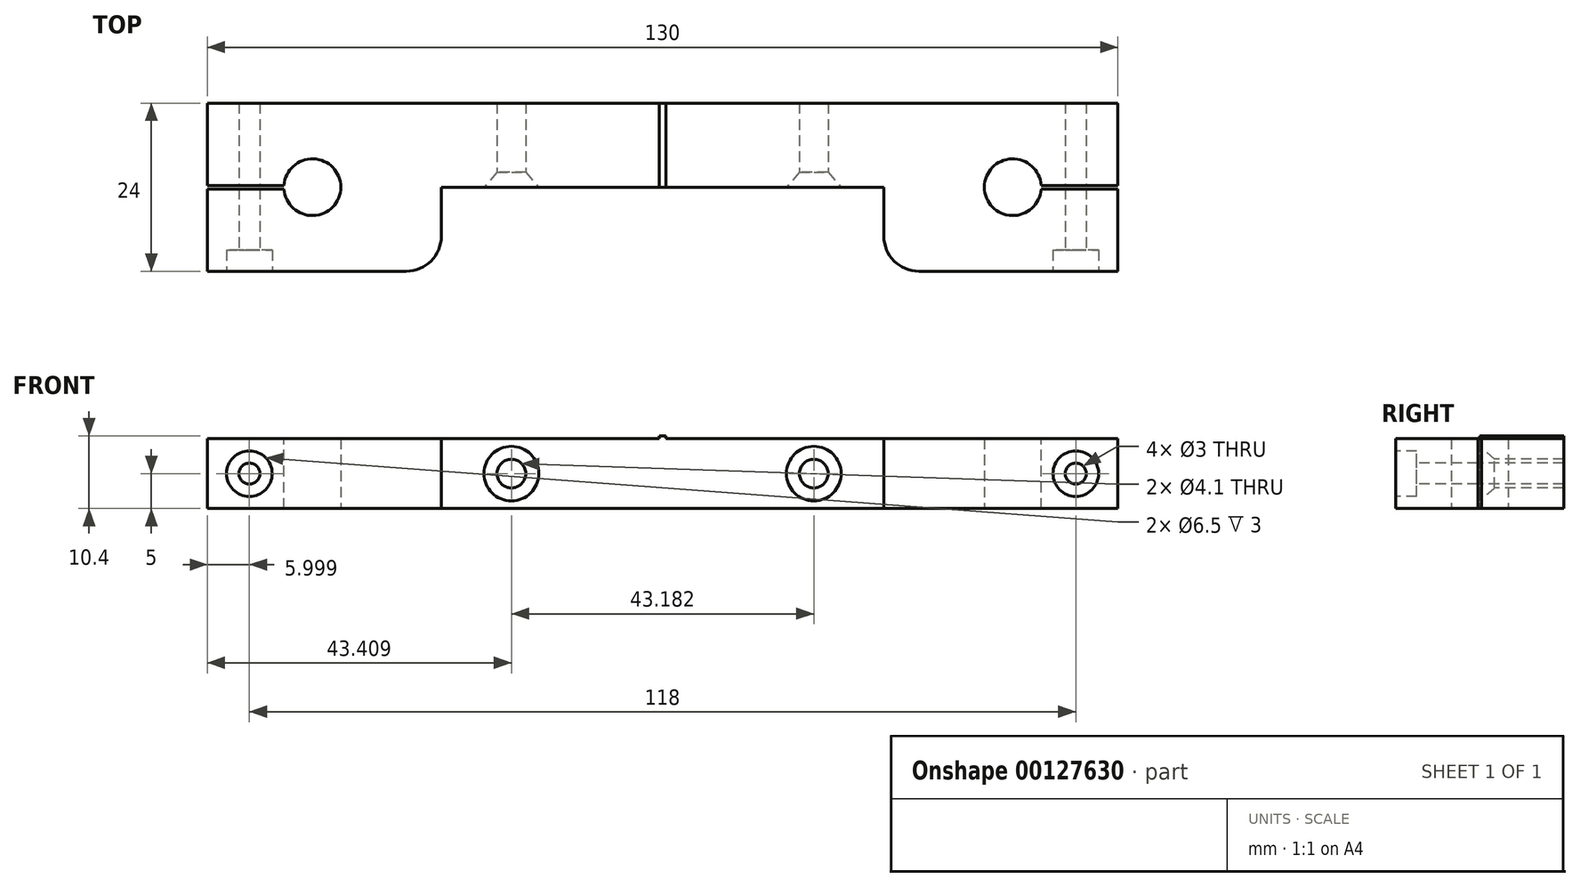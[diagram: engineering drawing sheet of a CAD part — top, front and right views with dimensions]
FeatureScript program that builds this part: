
annotation { "Feature Type Name" : "Feature", "Feature Type Description" : "" }
export const myFeature = defineFeature(function(context is Context, id is Id, definition is map)
    precondition{}
    {
        {
            var Q0;
            Q0=qCreatedBy(makeId("Top.planeOp"),FACE);
            var sketch = newSketch(context, id + "F0", { "sketchPlane" : qUnion([Q0])});
            skLineSegment(sketch, "E0.bottom", {"start": v(-62.4, -8.21) * mm, "end": v(67.6, -8.21) * mm});
            skLineSegment(sketch, "E0.top", {"start": v(-62.4, -32.21) * mm, "end": v(67.6, -32.21) * mm});
            skLineSegment(sketch, "E0.left", {"start": v(-62.4, -8.21) * mm, "end": v(-62.4, -32.21) * mm});
            skLineSegment(sketch, "E0.right", {"start": v(67.6, -8.21) * mm, "end": v(67.6, -32.21) * mm});
            skLineSegment(sketch, "E1", {"start": v(-62.4, -20.21) * mm, "end": v(67.6, -20.21) * mm, "construction": true});
            skLineSegment(sketch, "E2", {"start": v(-47.4, -8.21) * mm, "end": v(-47.4, -32.21) * mm, "construction": true});
            skCircle(sketch, "E3", {"center": v(-47.4, -20.21) * mm, "radius": 4.05 * mm});
            skCircle(sketch, "E4.1.0.0", {"center": v(52.6, -20.21) * mm, "radius": 4.05 * mm});
            skLineSegment(sketch, "E4.direction1", {"start": v(-47.4, -20.21) * mm, "end": v(52.6, -20.21) * mm, "construction": true});
            skPoint(sketch, "E5", {"position": v(2.6, -32.21) * mm});
            skLineSegment(sketch, "E6.bottom", {"start": v(-29, -32.21) * mm, "end": v(34.2, -32.21) * mm});
            skLineSegment(sketch, "E6.top", {"start": v(-29, -20.21) * mm, "end": v(34.2, -20.21) * mm});
            skLineSegment(sketch, "E6.left", {"start": v(-29, -32.21) * mm, "end": v(-29, -20.21) * mm});
            skLineSegment(sketch, "E6.right", {"start": v(34.2, -32.21) * mm, "end": v(34.2, -20.21) * mm});
            skPoint(sketch, "E7", {"position": v(2.6, -20.21) * mm});
            skSolve(sketch);
        }
        {
            var Q0;
            Q0=makeQuery(id+"F0.imprint","IMPRINT",FACE,{"disambiguationData":[TD([[makeQuery(id+"F0.imprint","IMPRINT",EDGE,{"derivedFrom":sQuery(id+"F0.wireOp",EDGE,"E0.bottom")}),-1.0]])]});
            extrude(context, id + "F1", {"entities" : qUnion([Q0]), "depth" : 10 * mm});
        }
        {
            var Q0;
            Q0=makeQuery(id+"F1.opExtrude","SWEPT_EDGE",EDGE,{"disambiguationData":[OSD([sQuery(id+"F0.wireOp",EDGE,"E0.top"),sQuery(id+"F0.wireOp",EDGE,"E6.bottom"),sQuery(id+"F0.wireOp",EDGE,"E6.right")])]});
            var Q1;
            Q1=makeQuery(id+"F1.opExtrude","SWEPT_EDGE",EDGE,{"disambiguationData":[OSD([sQuery(id+"F0.wireOp",EDGE,"E0.top"),sQuery(id+"F0.wireOp",EDGE,"E6.bottom"),sQuery(id+"F0.wireOp",EDGE,"E6.left")])]});
            fillet(context, id + "F2", {"entities" : qUnion([Q0, Q1]), "radius" : 5 * mm, "tangentPropagation" : true, "allowEdgeOverflow" : false});
        }
        {
            var Q0;
            Q0=makeQuery(id+"F1.opExtrude","SWEPT_FACE",FACE,{"disambiguationData":[OSD([sQuery(id+"F0.wireOp",EDGE,"E6.top")])]});
            var sketch = newSketch(context, id + "F3", { "sketchPlane" : qUnion([Q0])});
            skLineSegment(sketch, "E8", {"start": v(-29, 5) * mm, "end": v(34.2, 5) * mm, "construction": true});
            skLineSegment(sketch, "E9", {"start": v(-19, 10) * mm, "end": v(-19, 0) * mm, "construction": true});
            skLineSegment(sketch, "E10", {"start": v(24.2, 10) * mm, "end": v(24.2, 0) * mm, "construction": true});
            skPoint(sketch, "E11", {"position": v(-19, 5) * mm});
            skPoint(sketch, "E12", {"position": v(24.2, 5) * mm});
            skSolve(sketch);
        }
        {
            var Q0;
            Q0=sQuery(id+"F3.wireOp",VERTEX,"E11");
            var Q1;
            Q1=sQuery(id+"F3.wireOp",VERTEX,"E12");
            var Q2;
            Q2=makeQuery(id+"F1.opExtrude","SWEPT_BODY",BODY,{"disambiguationData":[OSD([sQuery(id+"F0.wireOp",EDGE,"E0.bottom"),sQuery(id+"F0.wireOp",EDGE,"E0.top"),sQuery(id+"F0.wireOp",EDGE,"E0.left"),sQuery(id+"F0.wireOp",EDGE,"E0.right"),sQuery(id+"F0.wireOp",EDGE,"E3"),sQuery(id+"F0.wireOp",EDGE,"E4.1.0.0"),sQuery(id+"F0.wireOp",EDGE,"E6.top"),sQuery(id+"F0.wireOp",EDGE,"E6.left"),sQuery(id+"F0.wireOp",EDGE,"E6.right")])]});
            hole(context, id + "F4", {"style" : HoleStyle.C_SINK, "endStyle" : HoleEndStyle.THROUGH, "holeDiameter" : 4.1 * mm, "cSinkDiameter" : 7.8 * mm, "cSinkAngle" : 82 * degree, "locations" : qUnion([Q0, Q1]), "scope" : qUnion([Q2]), "isTappedThrough" : true});
        }
        {
            var Q0;
            Q0=makeQuery(id+"F1.opExtrude","CAP_FACE",FACE,{"disambiguationData":[OSD([sQuery(id+"F0.wireOp",EDGE,"E0.bottom"),sQuery(id+"F0.wireOp",EDGE,"E0.top"),sQuery(id+"F0.wireOp",EDGE,"E0.left"),sQuery(id+"F0.wireOp",EDGE,"E0.right"),sQuery(id+"F0.wireOp",EDGE,"E3"),sQuery(id+"F0.wireOp",EDGE,"E4.1.0.0"),sQuery(id+"F0.wireOp",EDGE,"E6.top"),sQuery(id+"F0.wireOp",EDGE,"E6.left"),sQuery(id+"F0.wireOp",EDGE,"E6.right")])],"isStart":false});
            var sketch = newSketch(context, id + "F5", { "sketchPlane" : qUnion([Q0])});
            skPoint(sketch, "E13", {"position": v(2.6, -8.21) * mm});
            skPoint(sketch, "E14", {"position": v(2.6, -20.21) * mm});
            skLineSegment(sketch, "E15", {"start": v(2.1, -8.21) * mm, "end": v(2.1, -20.21) * mm});
            skLineSegment(sketch, "E16", {"start": v(3.1, -8.21) * mm, "end": v(3.1, -20.21) * mm});
            skSolve(sketch);
        }
        {
            var Q0;
            {var subQ0=sQuery(id+"F5.wireOp",EDGE,"E15");Q0=makeQuery(id+"F5.imprint","IMPRINT",FACE,{"disambiguationData":[TD([[makeQuery(id+"F5.imprint","IMPRINT",EDGE,{"derivedFrom":subQ0}),1.0]])]});}
            extrude(context, id + "F6", {"entities" : qUnion([Q0]), "operationType" : NewBodyOperationType.ADD, "depth" : 0.4 * mm});
        }
        {
            var Q0;
            {var subQ0=sQuery(id+"F0.wireOp",EDGE,"E3");var subQ1=sQuery(id+"F0.wireOp",EDGE,"E0.left");var subQ2=sQuery(id+"F0.wireOp",EDGE,"E0.top");var subQ3=sQuery(id+"F0.wireOp",EDGE,"E6.left");var subQ5=sQuery(id+"F0.wireOp",EDGE,"E0.bottom");var subQ6=sQuery(id+"F0.wireOp",EDGE,"E6.top");Q0=makeQuery(id+"F6.boolean.opBoolean","SPLIT",FACE,{"disambiguationData":[TD([makeQuery(id+"F1.opExtrude","SWEPT_FACE",FACE,{"disambiguationData":[OSD([subQ1])]})])],"derivedFrom":makeQuery(id+"F1.opExtrude","CAP_FACE",FACE,{"disambiguationData":[OSD([subQ5,subQ2,subQ1,sQuery(id+"F0.wireOp",EDGE,"E0.right"),subQ0,sQuery(id+"F0.wireOp",EDGE,"E4.1.0.0"),subQ6,subQ3,sQuery(id+"F0.wireOp",EDGE,"E6.right")])],"isStart":false})});}
            var sketch = newSketch(context, id + "F7", { "sketchPlane" : qUnion([Q0])});
            skLineSegment(sketch, "E17.bottom", {"start": v(-62.4, -19.96) * mm, "end": v(-51.44, -19.96) * mm});
            skLineSegment(sketch, "E17.top", {"start": v(-62.4, -20.46) * mm, "end": v(-51.44, -20.46) * mm});
            skLineSegment(sketch, "E17.left", {"start": v(-62.4, -19.96) * mm, "end": v(-62.4, -20.46) * mm});
            skLineSegment(sketch, "E17.right", {"start": v(-51.44, -19.96) * mm, "end": v(-51.44, -20.46) * mm});
            skCircle(sketch, "E18.0", {"center": v(-47.4, -20.21) * mm, "radius": 4.05 * mm});
            skPoint(sketch, "E19", {"position": v(-51.44, -20.21) * mm});
            skCircle(sketch, "E20.0", {"center": v(52.6, -20.21) * mm, "radius": 4.05 * mm});
            skLineSegment(sketch, "E21.bottom", {"start": v(56.64, -19.96) * mm, "end": v(67.6, -19.96) * mm});
            skLineSegment(sketch, "E21.top", {"start": v(56.64, -20.46) * mm, "end": v(67.6, -20.46) * mm});
            skLineSegment(sketch, "E21.left", {"start": v(56.64, -19.96) * mm, "end": v(56.64, -20.46) * mm});
            skLineSegment(sketch, "E21.right", {"start": v(67.6, -19.96) * mm, "end": v(67.6, -20.46) * mm});
            skPoint(sketch, "E22", {"position": v(56.64, -20.21) * mm});
            skSolve(sketch);
        }
        {
            var Q0;
            {var subQ1=sQuery(id+"F7.wireOp",EDGE,"E21.bottom");Q0=makeQuery(id+"F7.imprint","IMPRINT",FACE,{"disambiguationData":[TD([[makeQuery(id+"F7.imprint","IMPRINT",EDGE,{"derivedFrom":subQ1}),-1.0]])]});}
            var Q1;
            {var subQ0=sQuery(id+"F7.wireOp",EDGE,"E17.bottom");Q1=makeQuery(id+"F7.imprint","IMPRINT",FACE,{"disambiguationData":[TD([[makeQuery(id+"F7.imprint","IMPRINT",EDGE,{"derivedFrom":subQ0}),-1.0]])]});}
            var Q2;
            {var subQ0=sQuery(id+"F7.wireOp",EDGE,"E17.right");Q2=makeQuery(id+"F7.imprint","IMPRINT",FACE,{"disambiguationData":[TD([[makeQuery(id+"F7.imprint","IMPRINT",EDGE,{"derivedFrom":subQ0}),-1.0]])]});}
            var Q3;
            {var subQ0=sQuery(id+"F7.wireOp",EDGE,"E21.left");Q3=makeQuery(id+"F7.imprint","IMPRINT",FACE,{"disambiguationData":[TD([[makeQuery(id+"F7.imprint","IMPRINT",EDGE,{"derivedFrom":subQ0}),1.0]])]});}
            extrude(context, id + "F8", {"entities" : qUnion([Q0, Q1, Q2, Q3]), "operationType" : NewBodyOperationType.REMOVE, "oppositeDirection" : true, "depth" : 25 * mm});
        }
        {
            var Q0;
            {var subQ0=sQuery(id+"F0.wireOp",EDGE,"E0.top");Q0=makeQuery(id+"F1.opExtrude","SWEPT_FACE",FACE,{"disambiguationData":[OSD([subQ0]),TDD([makeQuery(id+"F0.imprint","IMPRINT",EDGE,{"disambiguationData":[TD([[makeQuery(id+"F0.imprint","INTERSECT",VERTEX,{"derivedFrom":[subQ0,sQuery(id+"F0.wireOp",EDGE,"E0.left")]}),-1.0]])],"derivedFrom":subQ0})])]});}
            var sketch = newSketch(context, id + "F9", { "sketchPlane" : qUnion([Q0])});
            skLineSegment(sketch, "E23", {"start": v(-62.4, 5) * mm, "end": v(-34, 5) * mm, "construction": true});
            skLineSegment(sketch, "E24", {"start": v(-56.4, 10) * mm, "end": v(-56.4, 0) * mm, "construction": true});
            skPoint(sketch, "E25", {"position": v(-56.4, 5) * mm});
            skLineSegment(sketch, "E26.0.0", {"start": v(67.6, 10) * mm, "end": v(39.2, 10) * mm});
            skLineSegment(sketch, "E26.0.1", {"start": v(39.2, 10) * mm, "end": v(39.2, 0) * mm});
            skLineSegment(sketch, "E26.0.2", {"start": v(39.2, 0) * mm, "end": v(67.6, 0) * mm});
            skLineSegment(sketch, "E26.0.3", {"start": v(67.6, 0) * mm, "end": v(67.6, 10) * mm});
            skLineSegment(sketch, "E27", {"start": v(67.6, 5) * mm, "end": v(39.2, 5) * mm, "construction": true});
            skLineSegment(sketch, "E28", {"start": v(61.6, 10) * mm, "end": v(61.6, 0) * mm, "construction": true});
            skPoint(sketch, "E29", {"position": v(61.6, 5) * mm});
            skSolve(sketch);
        }
        {
            var Q0;
            Q0=sQuery(id+"F9.wireOp",VERTEX,"E29");
            var Q1;
            Q1=sQuery(id+"F9.wireOp",VERTEX,"E25");
            var Q2;
            Q2=makeQuery(id+"F1.opExtrude","SWEPT_BODY",BODY,{"disambiguationData":[OSD([sQuery(id+"F0.wireOp",EDGE,"E0.bottom"),sQuery(id+"F0.wireOp",EDGE,"E0.top"),sQuery(id+"F0.wireOp",EDGE,"E0.left"),sQuery(id+"F0.wireOp",EDGE,"E0.right"),sQuery(id+"F0.wireOp",EDGE,"E3"),sQuery(id+"F0.wireOp",EDGE,"E4.1.0.0"),sQuery(id+"F0.wireOp",EDGE,"E6.top"),sQuery(id+"F0.wireOp",EDGE,"E6.left"),sQuery(id+"F0.wireOp",EDGE,"E6.right")])]});
            hole(context, id + "F10", {"style" : HoleStyle.C_BORE, "endStyle" : HoleEndStyle.THROUGH, "standardTappedOrClearance" : lookupTablePath({ "standard" : "ISO", "size" : "3", "type" : "Drilled" }), "standardBlindInLast" : lookupTablePath({ "standard" : "ISO", "size" : "3", "type" : "Drilled" }), "holeDiameter" : 3 * mm, "cBoreDiameter" : 6.5 * mm, "cBoreDepth" : 3 * mm, "locations" : qUnion([Q0, Q1]), "scope" : qUnion([Q2]), "isTappedThrough" : true});
        }
    });
